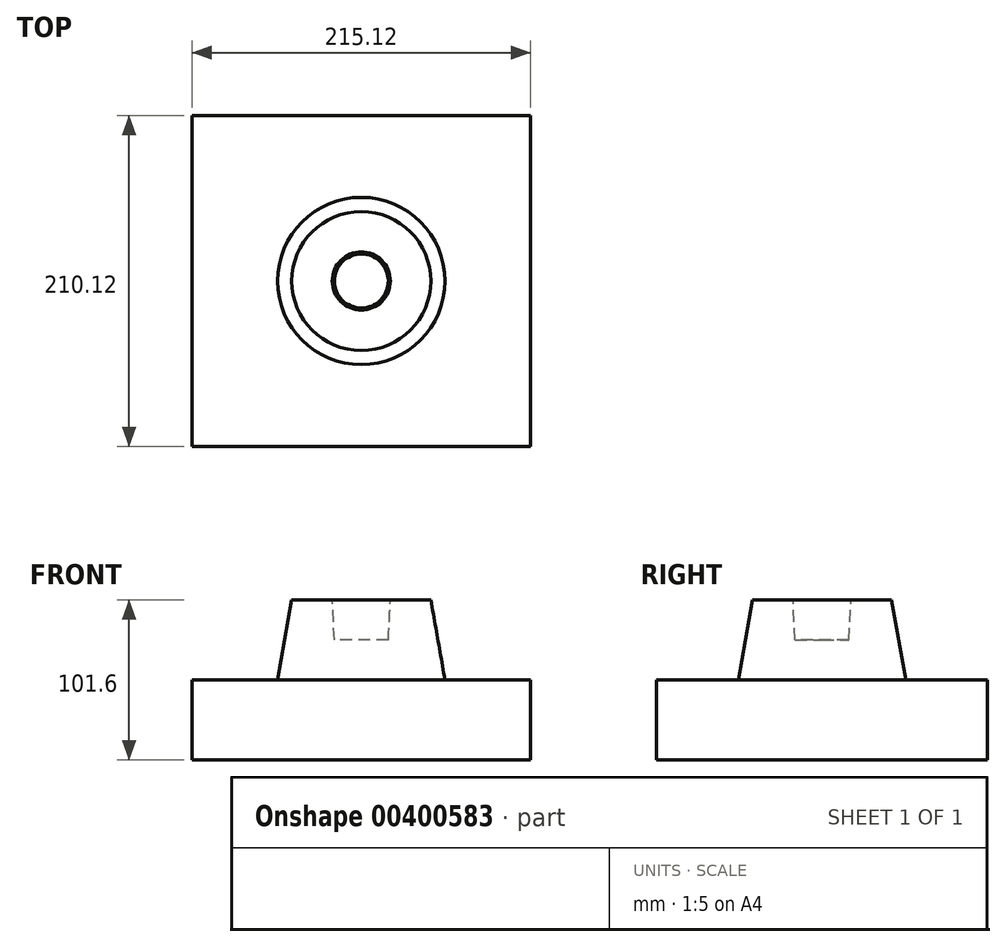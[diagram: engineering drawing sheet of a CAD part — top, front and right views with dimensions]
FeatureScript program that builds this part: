
annotation { "Feature Type Name" : "Feature", "Feature Type Description" : "" }
export const myFeature = defineFeature(function(context is Context, id is Id, definition is map)
    precondition{}
    {
        {
            var Q0;
            Q0=qCreatedBy(makeId("Top.planeOp"),FACE);
            var sketch = newSketch(context, id + "F0", { "sketchPlane" : qUnion([Q0])});
            skLineSegment(sketch, "E0.bottom", {"start": v(107.56, 105.06) * mm, "end": v(-107.56, 105.06) * mm});
            skLineSegment(sketch, "E0.top", {"start": v(107.56, -105.06) * mm, "end": v(-107.56, -105.06) * mm});
            skLineSegment(sketch, "E0.left", {"start": v(107.56, 105.06) * mm, "end": v(107.56, -105.06) * mm});
            skLineSegment(sketch, "E0.right", {"start": v(-107.56, 105.06) * mm, "end": v(-107.56, -105.06) * mm});
            skPoint(sketch, "E0.middle", {"position": v(0, 0) * mm});
            skSolve(sketch);
        }
        {
            var Q0;
            Q0=makeQuery(id+"F0.imprint","IMPRINT",FACE,{"disambiguationData":[TD([[makeQuery(id+"F0.imprint","IMPRINT",EDGE,{"derivedFrom":sQuery(id+"F0.wireOp",EDGE,"E0.bottom")}),1.0]])]});
            extrude(context, id + "F1", {"entities" : qUnion([Q0]), "depth" : 50.8 * mm});
        }
        {
            var Q0;
            Q0=makeQuery(id+"F1.opExtrude","CAP_FACE",FACE,{"disambiguationData":[OSD([sQuery(id+"F0.wireOp",EDGE,"E0.bottom"),sQuery(id+"F0.wireOp",EDGE,"E0.top"),sQuery(id+"F0.wireOp",EDGE,"E0.left"),sQuery(id+"F0.wireOp",EDGE,"E0.right")])],"isStart":false});
            var sketch = newSketch(context, id + "F2", { "sketchPlane" : qUnion([Q0])});
            skCircle(sketch, "E1", {"center": v(0, 0) * mm, "radius": 53.13 * mm});
            skSolve(sketch);
        }
        {
            var Q0;
            Q0=makeQuery(id+"F2.imprint","IMPRINT",FACE,{"disambiguationData":[TD([[makeQuery(id+"F2.imprint","IMPRINT",EDGE,{"derivedFrom":sQuery(id+"F2.wireOp",EDGE,"E1")}),1.0]])]});
            extrude(context, id + "F3", {"entities" : qUnion([Q0]), "operationType" : NewBodyOperationType.ADD, "depth" : 50.8 * mm, "hasDraft" : true, "draftAngle" : 10 * degree, "draftPullDirection" : true});
        }
        {
            var Q0;
            Q0=makeQuery(id+"F3.opExtrude","CAP_FACE",FACE,{"disambiguationData":[OSD([sQuery(id+"F2.wireOp",EDGE,"E1")])],"isStart":false});
            var sketch = newSketch(context, id + "F4", { "sketchPlane" : qUnion([Q0])});
            skSolve(sketch);
        }
        {
            var Q0;
            Q0=makeQuery(id+"F4.imprint","IMPRINT",FACE,{"disambiguationData":[TD([[makeQuery(id+"F4.imprint","IMPRINT",EDGE,{"derivedFrom":makeQuery(id+"F3.opExtrude","CAP_EDGE",EDGE,{"disambiguationData":[OSD([sQuery(id+"F2.wireOp",EDGE,"E1")])],"isStart":false})}),1.0]])]});
            var sketch = newSketch(context, id + "F5", { "sketchPlane" : qUnion([Q0])});
            skCircle(sketch, "E2", {"center": v(0, 0) * mm, "radius": 18.45 * mm});
            skSolve(sketch);
        }
        {
            var Q0;
            Q0=makeQuery(id+"F5.imprint","IMPRINT",FACE,{"disambiguationData":[TD([[makeQuery(id+"F5.imprint","IMPRINT",EDGE,{"derivedFrom":sQuery(id+"F5.wireOp",EDGE,"E2")}),1.0]])]});
            extrude(context, id + "F6", {"entities" : qUnion([Q0]), "operationType" : NewBodyOperationType.REMOVE, "oppositeDirection" : true, "depth" : 25.4 * mm, "hasDraft" : true, "draftAngle" : 3 * degree, "draftPullDirection" : true});
        }
    });
